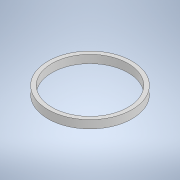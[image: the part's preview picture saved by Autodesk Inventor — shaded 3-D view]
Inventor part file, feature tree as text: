
AUTODESK INVENTOR PART (.ipt)
format: ipt  version: 2022.3 (Build 263350000, 350)  size: 104,960 bytes
history: native  units: mm
features: extrude x1, sketch x1
ambient origin geometry x8: Origin, YZ Plane, XZ Plane, XY Plane, X Axis, Y Axis, Z Axis, Center Point
bodies: Solid1 (feature_tree)
feature tree (2):
  extrude  "Extrusion1"  Depth=4.0mm
  sketch  "Sketch1"  dims[d0=41.9mm d1=2.0mm d2=4.0mm d3=0.0mm]
